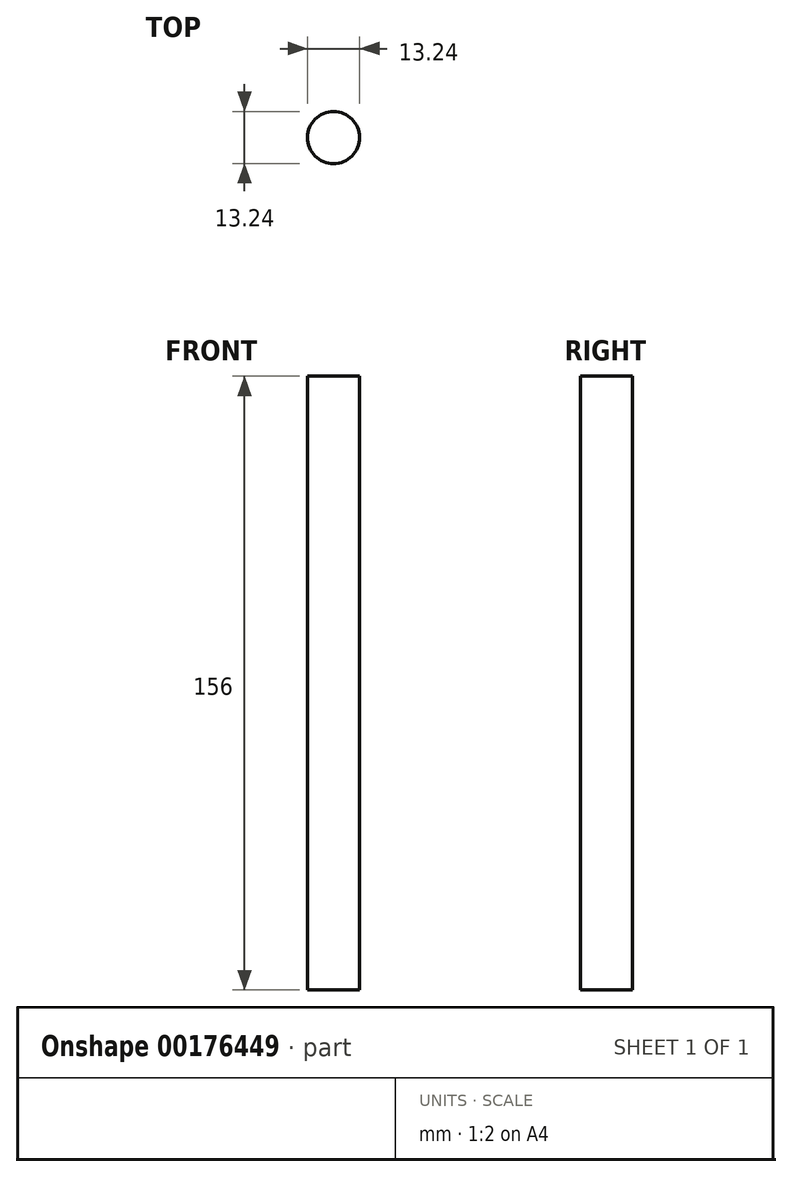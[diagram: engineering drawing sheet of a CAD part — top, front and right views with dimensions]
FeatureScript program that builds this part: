
annotation { "Feature Type Name" : "Feature", "Feature Type Description" : "" }
export const myFeature = defineFeature(function(context is Context, id is Id, definition is map)
    precondition{}
    {
        {
            var Q0;
            Q0=qCreatedBy(makeId("Top.planeOp"),FACE);
            var sketch = newSketch(context, id + "F0", { "sketchPlane" : qUnion([Q0])});
            skCircle(sketch, "E0", {"center": v(0, 0) * mm, "radius": 6.62 * mm});
            skSolve(sketch);
        }
        {
            var Q0;
            Q0=makeQuery(id+"F0.imprint","IMPRINT",FACE,{"disambiguationData":[TD([[makeQuery(id+"F0.imprint","IMPRINT",EDGE,{"derivedFrom":sQuery(id+"F0.wireOp",EDGE,"E0")}),1.0]])]});
            extrude(context, id + "F1", {"entities" : qUnion([Q0]), "depth" : 156 * mm});
        }
    });
